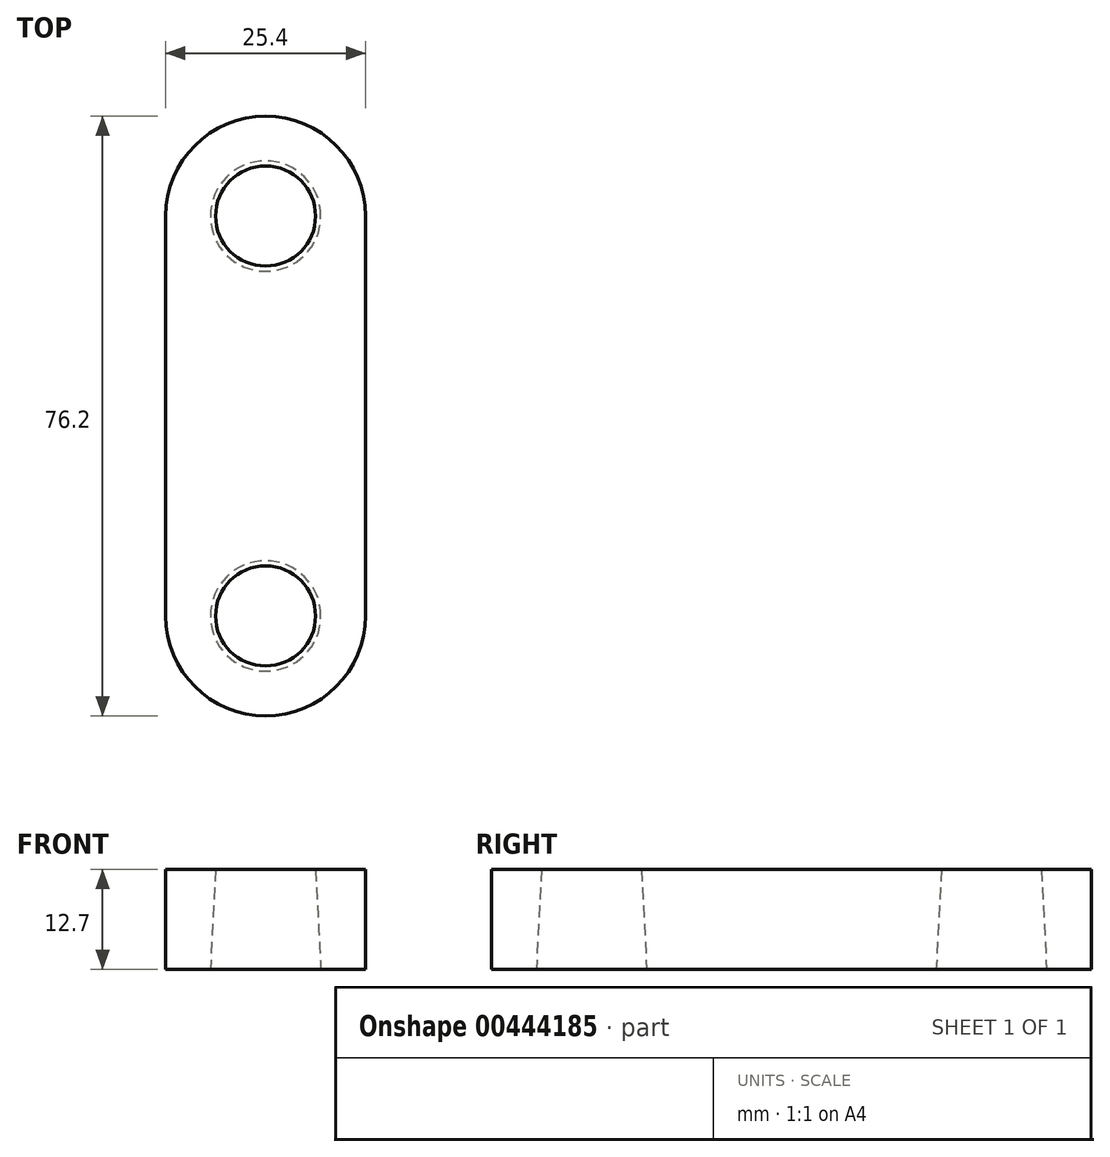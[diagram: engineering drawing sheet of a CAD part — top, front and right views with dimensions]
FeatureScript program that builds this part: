
annotation { "Feature Type Name" : "Feature", "Feature Type Description" : "" }
export const myFeature = defineFeature(function(context is Context, id is Id, definition is map)
    precondition{}
    {
        {
            var Q0;
            Q0=qCreatedBy(makeId("Top.planeOp"),FACE);
            var sketch = newSketch(context, id + "F0", { "sketchPlane" : qUnion([Q0])});
            skArc(sketch, "E0", {"start": v(-12.7, -25.4) * mm, "mid": v(0, -38.1) * mm, "end": v(12.7, -25.4) * mm});
            skLineSegment(sketch, "E1", {"start": v(12.7, -25.4) * mm, "end": v(12.7, 0) * mm});
            skLineSegment(sketch, "E2", {"start": v(-12.7, -25.4) * mm, "end": v(-12.7, 0) * mm});
            skLineSegment(sketch, "E3.MirrorCS", {"start": v(-12.7, 25.4) * mm, "end": v(-12.7, 0) * mm});
            skArc(sketch, "E4.MirrorCS", {"start": v(-12.7, 25.4) * mm, "mid": v(0, 38.1) * mm, "end": v(12.7, 25.4) * mm});
            skLineSegment(sketch, "E5.MirrorCS", {"start": v(12.7, 25.4) * mm, "end": v(12.7, 0) * mm});
            skSolve(sketch);
        }
        {
            var Q0;
            Q0 = qSketchRegion(id + "F0", true);
            extrude(context, id + "F1", {"entities" : qUnion([Q0]), "depth" : 12.7 * mm});
        }
        {
            var Q0;
            Q0=makeQuery(id+"F1.opExtrude","CAP_FACE",FACE,{"disambiguationData":[OSD([sQuery(id+"F0.wireOp",EDGE,"E0"),sQuery(id+"F0.wireOp",EDGE,"E1"),sQuery(id+"F0.wireOp",EDGE,"E2"),sQuery(id+"F0.wireOp",EDGE,"E3.MirrorCS"),sQuery(id+"F0.wireOp",EDGE,"E4.MirrorCS"),sQuery(id+"F0.wireOp",EDGE,"E5.MirrorCS")])],"isStart":false});
            var sketch = newSketch(context, id + "F2", { "sketchPlane" : qUnion([Q0])});
            skCircle(sketch, "E6", {"center": v(0, 25.4) * mm, "radius": 6.35 * mm});
            skCircle(sketch, "E7.MirrorC", {"center": v(0, -25.4) * mm, "radius": 6.35 * mm});
            skSolve(sketch);
        }
        {
            var Q0;
            Q0 = qSketchRegion(id + "F2", true);
            extrude(context, id + "F3", {"entities" : qUnion([Q0]), "operationType" : NewBodyOperationType.REMOVE, "oppositeDirection" : true, "depth" : 25.4 * mm, "hasDraft" : true, "draftAngle" : 3 * degree});
        }
    });
